# Revit family: NBS_Allermuir_DmstcChrs_Mozaik
name_source: partatom
category: Furniture
revit_build: Autodesk Revit 2016 (Build: 20161004_0715(x64)
units: mm (PartAtom-declared; Revit-internal decimal feet)

## family parameters
Always vertical = Yes
Cut with Voids When Loaded = No
Room Calculation Point = No
Shared = No
Work Plane-Based = No

## types (5) — shared parameters
AssetType = Moveable
Category = Pr_40_50_12_22:Dining chairs
CodePerformance = BS EN 16139:2013 level 1
DurationUnit = year
EnvironmentalProductDeclaration = http://www.thesenatorgroup.com
ExpectedLife = 5
Features = Traditional carcass construction, fully upholstred, wire frame finished in black powder coat, plastic glides, wire frame available in white, coral or pebble powder coat, two tone upholstery
FrameColourOptions = White, coral, pebble
FrameFinishOptions = Two tone upholstery
FramesColour = Black
FramesFinish = Powder coat
FramesMaterial = Steel
IfcExportAs = IfcFurnitureType
IfcExportType = SOFA
IntegralAccessories = Plastic glides
IsBuiltIn = No
LegMaterial = NBS_Concept
ManufacturerName = Allermuir
ManufacturerURL = http://www.thesenatorgroup.com
ModelReference = Mozaik
NBSCertification = www.nationalbimlibrary.com/cert/g1kzdwom
NBSDescription = Domestic chairs
NBSReference = 45-35-20/365
ProductInformation = http://www.thesenatorgroup.com
SeatMaterial = NBS_Concept
SeatsAndBacksFinish = Fully upholstered
Status = UNSET
Uniclass2015Code = Pr_40_50_12_22
Uniclass2015Title = Dining chairs
Uniclass2015Version = Products v1.9
Version = 1
WarrantyDescription = Allermuir warrant that its manufactured products are free from manufacturing defects in materials or workmanship for a period of five years
WarrantyDurationParts = 5
WarrantyDurationUnit = year
zero-valued in all types: HighestSeatingHeight, LowestSeatingHeight

## per-type parameters (varying)
| type | BIMObjectName | Description | ModelNumber | Name | NominalDepth | NominalHeight | NominalLength | NominalWidth | SeatingHeight | Size |
| MZK101 | NBS_Allermuir_DomesticChairs_Mozaik_MZK203 | High rectangular bench | MZK203 | DomesticChairs_Mozaik_MZK203_Allermuir | 435 mm  [stored 1.42717 ft] | 420 mm | 435 mm  [stored 1.42717 ft] | 435 mm  [stored 1.42717 ft] | 595 mm  [stored 1.9521 ft] | 865 x 435 x 595 mm |
| MZK201 | NBS_Allermuir_DomesticChairs_Mozaik_MZK201 | High square stool, small | MZK201 | DomesticChairs_Mozaik_MZK201_Allermuir | 435 mm  [stored 1.42717 ft] | 595 mm  [stored 1.9521 ft] | 435 mm  [stored 1.42717 ft] | 435 mm  [stored 1.42717 ft] | 595 mm  [stored 1.9521 ft] | 435 x 435 x 595 mm |
| MZK102 | NBS_Allermuir_DomesticChairs_Mozaik_MZK102 | Low square stool, large | MZK102 | DomesticChairs_Mozaik_MZK102_Allermuir | 865 mm | 420 mm | 865 mm | 865 mm | 420 mm | 865 x 865 x 420 mm |
| MZK103 | NBS_Allermuir_DomesticChairs_Mozaik_MZK103 | Low rectangular bench | MZK103 | DomesticChairs_Mozaik_MZK103_Allermuir | 435 mm  [stored 1.42717 ft] | 420 mm | 865 mm | 435 mm  [stored 1.42717 ft] | 420 mm | 865 x 435 x 420 mm |
| MZK203 | NBS_Allermuir_DomesticChairs_Mozaik_MZK203 | High rectangular bench | MZK203 | DomesticChairs_Mozaik_MZK203_Allermuir | 435 mm  [stored 1.42717 ft] | 595 mm  [stored 1.9521 ft] | 865 mm | 435 mm  [stored 1.42717 ft] | 595 mm  [stored 1.9521 ft] | 865 x 435 x 595 mm |

note: [stored X ft] marks values corroborated as IEEE doubles in the binary element streams (Revit-internal decimal feet)

## geometry (parser evidence)
native form markers: Sweep x3
no freeform markers — native parametric forms only
